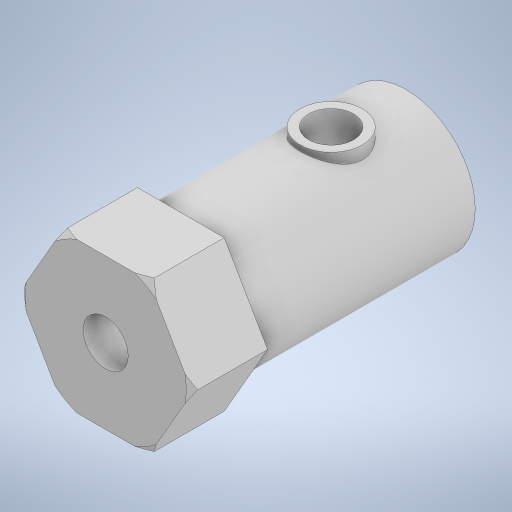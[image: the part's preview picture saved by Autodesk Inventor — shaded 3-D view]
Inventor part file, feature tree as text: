
AUTODESK INVENTOR PART (.ipt)
format: ipt  version: 2024 (Build 280153000, 153)  size: 493,056 bytes
history: native  units: mm
features: sketch x6, extrude x5, revolve x1, chamfer x1, plane x1
ambient origin geometry x8: Origin, YZ Plane, XZ Plane, XY Plane, X Axis, Y Axis, Z Axis, Center Point
bodies: Body1 (feature_tree)
feature tree (14):
  extrude  "Extrusion6"  Depth=6.0mm TaperAngle=0.0deg
  extrude  "Extrusion7"  Depth=5.15mm
  revolve  "Revolution1"  [1 undecoded]
  chamfer  "Chamfer3"  Distance=18.0mm
  extrude  "Extrusion8"  Depth=6.981317mm
  extrude  "Extrusion11"  Depth=0.125mm
  plane  "Work Plane2"
  extrude  "Extrusion12"  Depth=10.0mm TaperAngle=45.0deg
  sketch  "Sketch7"  dims[d24=12.0mm d25=6.0mm d26=0.0mm]
  sketch  "Sketch8"  dims[d27=11.0mm d28=5.15mm]
  sketch  "Sketch9"  dims[d29=4.5mm d30=1.573213mm d31=18.0mm d32=0.0mm]
  sketch  "Sketch10"  dims[d33=0.5mm d35=6.981317mm]
  sketch  "Sketch13"  dims[d38=90.0deg d39=0.125mm]
  sketch  "Sketch14"  dims[d40=0.104887mm d41=1.0mm d42=2.0mm d43=45.0deg d44=3.6mm d45=0.0mm d46=0.0mm d55=3.6mm d56=18.0mm d57=0.0mm d58=0.0mm d59=0.0mm d60=-4.0mm d61=5.0mm d62=18.0mm d63=10.0mm d64=0.0mm]
note: 1 required parameter value undecoded (feature->parameter linkage not recoverable at this tier; creation-order binding heuristic only, values carry confidence <= 0.55)
